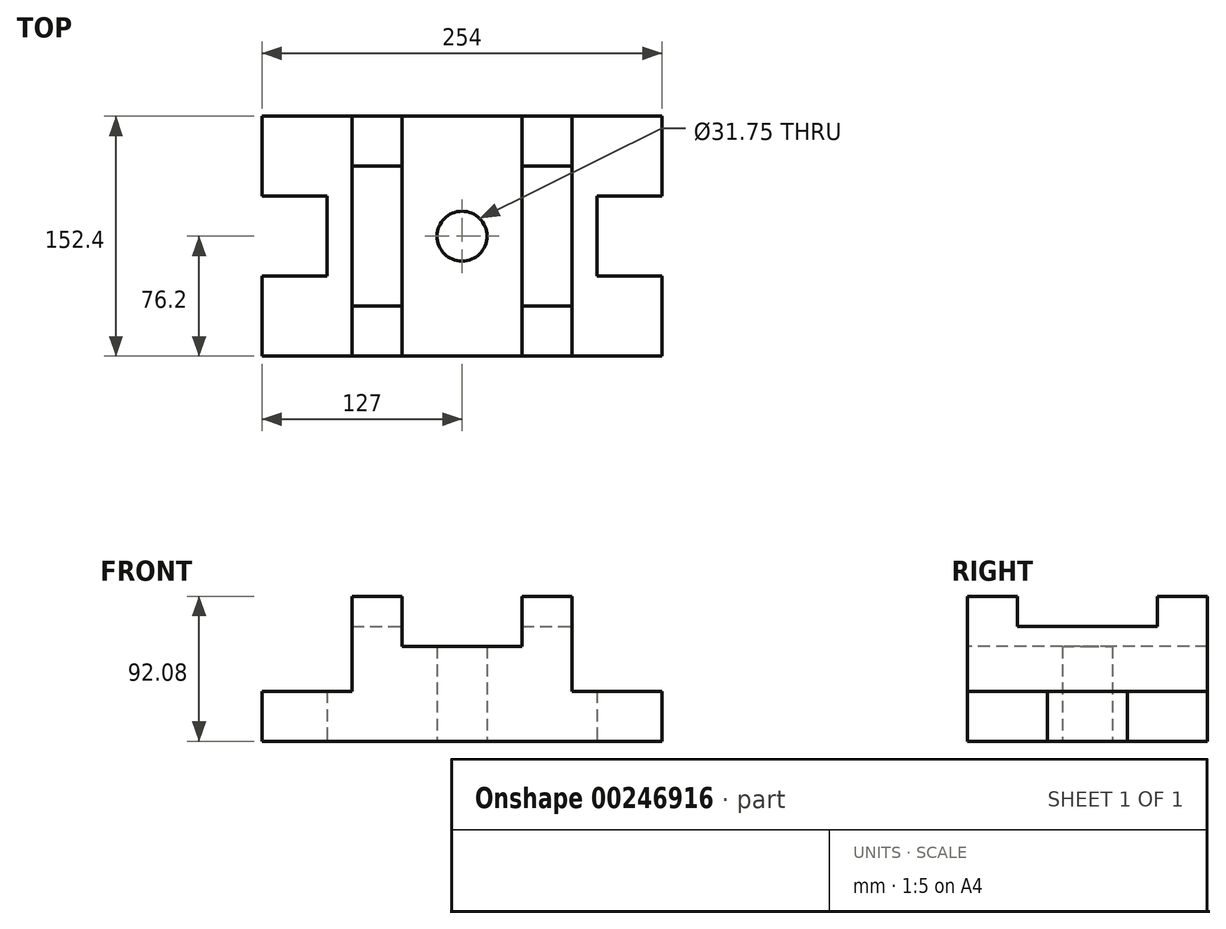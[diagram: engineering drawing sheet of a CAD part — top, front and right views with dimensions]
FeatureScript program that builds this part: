
annotation { "Feature Type Name" : "Feature", "Feature Type Description" : "" }
export const myFeature = defineFeature(function(context is Context, id is Id, definition is map)
    precondition{}
    {
        {
            var Q0;
            Q0=qCreatedBy(makeId("Top.planeOp"),FACE);
            var sketch = newSketch(context, id + "F0", { "sketchPlane" : qUnion([Q0])});
            skCircle(sketch, "E0", {"center": v(0, 0) * mm, "radius": 15.88 * mm});
            skLineSegment(sketch, "E1", {"start": v(-38.1, -76.2) * mm, "end": v(38.1, -76.2) * mm});
            skPoint(sketch, "E2", {"position": v(0, -76.2) * mm});
            skLineSegment(sketch, "E3", {"start": v(-38.1, 76.2) * mm, "end": v(38.1, 76.2) * mm});
            skPoint(sketch, "E4", {"position": v(0, 76.2) * mm});
            skLineSegment(sketch, "E5", {"start": v(-38.1, 76.2) * mm, "end": v(-38.1, -76.2) * mm});
            skLineSegment(sketch, "E6", {"start": v(38.1, 76.2) * mm, "end": v(38.1, -76.2) * mm});
            skLineSegment(sketch, "E7", {"start": v(-38.1, 76.2) * mm, "end": v(-69.85, 76.2) * mm});
            skLineSegment(sketch, "E8", {"start": v(-69.85, 76.2) * mm, "end": v(-69.85, 44.45) * mm});
            skLineSegment(sketch, "E9", {"start": v(-69.85, 44.45) * mm, "end": v(-38.1, 44.45) * mm});
            skLineSegment(sketch, "E10", {"start": v(-38.1, 44.45) * mm, "end": v(-38.1, 76.2) * mm});
            skLineSegment(sketch, "E11", {"start": v(38.1, 76.2) * mm, "end": v(69.85, 76.2) * mm});
            skLineSegment(sketch, "E12", {"start": v(69.85, 76.2) * mm, "end": v(69.85, 44.45) * mm});
            skLineSegment(sketch, "E13", {"start": v(69.85, 44.45) * mm, "end": v(38.1, 44.45) * mm});
            skLineSegment(sketch, "E14", {"start": v(38.1, 44.45) * mm, "end": v(38.1, 76.2) * mm});
            skLineSegment(sketch, "E15", {"start": v(-38.1, -76.2) * mm, "end": v(-69.85, -76.2) * mm});
            skLineSegment(sketch, "E16", {"start": v(-69.85, -76.2) * mm, "end": v(-69.85, -44.45) * mm});
            skLineSegment(sketch, "E17", {"start": v(-69.85, -44.45) * mm, "end": v(-38.1, -44.45) * mm});
            skLineSegment(sketch, "E18", {"start": v(-38.1, -44.45) * mm, "end": v(-38.1, -76.2) * mm});
            skLineSegment(sketch, "E19", {"start": v(38.1, -76.2) * mm, "end": v(69.85, -76.2) * mm});
            skLineSegment(sketch, "E20", {"start": v(69.85, -76.2) * mm, "end": v(69.85, -44.45) * mm});
            skLineSegment(sketch, "E21", {"start": v(69.85, -44.45) * mm, "end": v(38.1, -44.45) * mm});
            skLineSegment(sketch, "E22", {"start": v(38.1, -44.45) * mm, "end": v(38.1, -76.2) * mm});
            skLineSegment(sketch, "E23", {"start": v(-69.85, 44.45) * mm, "end": v(-69.85, -44.45) * mm});
            skLineSegment(sketch, "E24", {"start": v(69.85, 44.45) * mm, "end": v(69.85, -44.45) * mm});
            skLineSegment(sketch, "E25", {"start": v(69.85, 76.2) * mm, "end": v(127, 76.2) * mm});
            skLineSegment(sketch, "E26", {"start": v(127, 76.2) * mm, "end": v(127, 25.4) * mm});
            skLineSegment(sketch, "E27", {"start": v(127, -76.2) * mm, "end": v(69.85, -76.2) * mm});
            skLineSegment(sketch, "E28", {"start": v(-69.85, 76.2) * mm, "end": v(-127, 76.2) * mm});
            skLineSegment(sketch, "E29", {"start": v(-127, 76.2) * mm, "end": v(-127, 25.4) * mm});
            skLineSegment(sketch, "E30", {"start": v(-127, -76.2) * mm, "end": v(-69.85, -76.2) * mm});
            skLineSegment(sketch, "E31", {"start": v(127, 25.4) * mm, "end": v(85.72, 25.4) * mm});
            skLineSegment(sketch, "E32", {"start": v(85.72, 25.4) * mm, "end": v(85.72, -25.4) * mm});
            skLineSegment(sketch, "E33", {"start": v(85.72, -25.4) * mm, "end": v(127, -25.4) * mm});
            skLineSegment(sketch, "E34", {"start": v(-127, 25.4) * mm, "end": v(-85.73, 25.4) * mm});
            skLineSegment(sketch, "E35", {"start": v(-85.73, 25.4) * mm, "end": v(-85.73, -25.4) * mm});
            skLineSegment(sketch, "E36", {"start": v(-85.73, -25.4) * mm, "end": v(-127, -25.4) * mm});
            skLineSegment(sketch, "E37.trimOffspring", {"start": v(-127, -25.4) * mm, "end": v(-127, -76.2) * mm});
            skLineSegment(sketch, "E38.trimOffspring", {"start": v(127, -25.4) * mm, "end": v(127, -76.2) * mm});
            skSolve(sketch);
        }
        {
            var Q0;
            Q0=makeQuery(id+"F0.imprint","IMPRINT",FACE,{"disambiguationData":[TD([[makeQuery(id+"F0.imprint","IMPRINT",EDGE,{"derivedFrom":sQuery(id+"F0.wireOp",EDGE,"E7")}),1.0]])]});
            var Q1;
            Q1=makeQuery(id+"F0.imprint","IMPRINT",FACE,{"disambiguationData":[TD([[makeQuery(id+"F0.imprint","IMPRINT",EDGE,{"derivedFrom":sQuery(id+"F0.wireOp",EDGE,"E11")}),-1.0]])]});
            var Q2;
            Q2=makeQuery(id+"F0.imprint","IMPRINT",FACE,{"disambiguationData":[TD([[makeQuery(id+"F0.imprint","IMPRINT",EDGE,{"derivedFrom":sQuery(id+"F0.wireOp",EDGE,"E15")}),-1.0]])]});
            var Q3;
            Q3=makeQuery(id+"F0.imprint","IMPRINT",FACE,{"disambiguationData":[TD([[makeQuery(id+"F0.imprint","IMPRINT",EDGE,{"derivedFrom":sQuery(id+"F0.wireOp",EDGE,"E19")}),1.0]])]});
            var Q4;
            Q4=makeQuery(id+"F0.imprint","IMPRINT",FACE,{"disambiguationData":[TD([[makeQuery(id+"F0.imprint","IMPRINT",EDGE,{"derivedFrom":sQuery(id+"F0.wireOp",EDGE,"E8")}),-1.0]])]});
            var Q5;
            Q5=makeQuery(id+"F0.imprint","IMPRINT",FACE,{"disambiguationData":[TD([[makeQuery(id+"F0.imprint","IMPRINT",EDGE,{"derivedFrom":sQuery(id+"F0.wireOp",EDGE,"E12")}),1.0]])]});
            var Q6;
            Q6=makeQuery(id+"F0.imprint","IMPRINT",FACE,{"disambiguationData":[TD([[makeQuery(id+"F0.imprint","IMPRINT",EDGE,{"derivedFrom":sQuery(id+"F0.wireOp",EDGE,"E0")}),-1.0]])]});
            var Q7;
            Q7=makeQuery(id+"F0.imprint","IMPRINT",FACE,{"disambiguationData":[TD([[makeQuery(id+"F0.imprint","IMPRINT",EDGE,{"derivedFrom":sQuery(id+"F0.wireOp",EDGE,"E5")}),-1.0]])]});
            var Q8;
            Q8=makeQuery(id+"F0.imprint","IMPRINT",FACE,{"disambiguationData":[TD([[makeQuery(id+"F0.imprint","IMPRINT",EDGE,{"derivedFrom":sQuery(id+"F0.wireOp",EDGE,"E6")}),1.0]])]});
            extrude(context, id + "F1", {"entities" : qUnion([Q0, Q1, Q2, Q3, Q4, Q5, Q6, Q7, Q8]), "depth" : 92.07 * mm});
        }
        {
            var Q0;
            Q0=makeQuery(id+"F1.opExtrude","SWEPT_FACE",FACE,{"disambiguationData":[OSD([sQuery(id+"F0.wireOp",EDGE,"E1"),sQuery(id+"F0.wireOp",EDGE,"E15"),sQuery(id+"F0.wireOp",EDGE,"E19"),sQuery(id+"F0.wireOp",EDGE,"E27"),sQuery(id+"F0.wireOp",EDGE,"E30")])]});
            var sketch = newSketch(context, id + "F2", { "sketchPlane" : qUnion([Q0])});
            skLineSegment(sketch, "E39", {"start": v(-127, 0) * mm, "end": v(-127, 31.75) * mm});
            skLineSegment(sketch, "E40", {"start": v(-127, 31.75) * mm, "end": v(-69.85, 31.75) * mm});
            skLineSegment(sketch, "E41", {"start": v(-69.85, 31.75) * mm, "end": v(-69.85, 0) * mm});
            skLineSegment(sketch, "E42", {"start": v(127, 0) * mm, "end": v(127, 31.75) * mm});
            skLineSegment(sketch, "E43", {"start": v(127, 31.75) * mm, "end": v(69.85, 31.75) * mm});
            skLineSegment(sketch, "E44", {"start": v(69.85, 31.75) * mm, "end": v(69.85, 0) * mm});
            skLineSegment(sketch, "E45", {"start": v(69.85, 0) * mm, "end": v(127, 0) * mm});
            skLineSegment(sketch, "E46", {"start": v(-69.85, 0) * mm, "end": v(-127, 0) * mm});
            skLineSegment(sketch, "E47.bottom", {"start": v(-127, 31.75) * mm, "end": v(-127, 31.75) * mm});
            skLineSegment(sketch, "E47.top", {"start": v(-127, 92.08) * mm, "end": v(-127, 92.08) * mm});
            skLineSegment(sketch, "E47.left", {"start": v(-127, 31.75) * mm, "end": v(-127, 92.08) * mm});
            skLineSegment(sketch, "E47.right", {"start": v(-127, 31.75) * mm, "end": v(-127, 92.08) * mm});
            skLineSegment(sketch, "E48", {"start": v(-69.85, 31.75) * mm, "end": v(-69.85, 92.08) * mm});
            skLineSegment(sketch, "E49", {"start": v(-69.85, 92.08) * mm, "end": v(-127, 92.08) * mm});
            skLineSegment(sketch, "E50", {"start": v(127, 31.75) * mm, "end": v(127, 92.08) * mm});
            skLineSegment(sketch, "E51", {"start": v(127, 92.07) * mm, "end": v(69.85, 92.07) * mm});
            skLineSegment(sketch, "E52", {"start": v(69.85, 92.07) * mm, "end": v(69.85, 31.75) * mm});
            skLineSegment(sketch, "E53", {"start": v(-69.85, 92.08) * mm, "end": v(-38.1, 92.08) * mm});
            skLineSegment(sketch, "E54", {"start": v(-38.1, 92.08) * mm, "end": v(-38.1, 60.24) * mm});
            skLineSegment(sketch, "E55", {"start": v(-38.1, 60.24) * mm, "end": v(38.1, 60.24) * mm});
            skLineSegment(sketch, "E56", {"start": v(38.1, 60.24) * mm, "end": v(38.1, 92.08) * mm});
            skLineSegment(sketch, "E57", {"start": v(38.1, 92.08) * mm, "end": v(69.85, 92.07) * mm});
            skLineSegment(sketch, "E58", {"start": v(-38.1, 92.08) * mm, "end": v(38.1, 92.08) * mm});
            skSolve(sketch);
        }
        {
            var Q0;
            Q0=makeQuery(id+"F2.imprint","IMPRINT",FACE,{"disambiguationData":[TD([[makeQuery(id+"F2.imprint","IMPRINT",EDGE,{"derivedFrom":sQuery(id+"F2.wireOp",EDGE,"E54")}),1.0]])]});
            var Q1;
            Q1=makeQuery(id+"F2.imprint","IMPRINT",FACE,{"disambiguationData":[TD([[makeQuery(id+"F2.imprint","IMPRINT",EDGE,{"derivedFrom":sQuery(id+"F2.wireOp",EDGE,"E40")}),1.0]])]});
            var Q2;
            Q2=makeQuery(id+"F2.imprint","IMPRINT",FACE,{"disambiguationData":[TD([[makeQuery(id+"F2.imprint","IMPRINT",EDGE,{"derivedFrom":sQuery(id+"F2.wireOp",EDGE,"E43")}),-1.0]])]});
            extrude(context, id + "F3", {"entities" : qUnion([Q0, Q1, Q2]), "operationType" : NewBodyOperationType.REMOVE, "endBound" : BoundingType.THROUGH_ALL, "oppositeDirection" : true, "depth" : 25.4 * mm});
        }
        {
            var Q0;
            Q0=makeQuery(id+"F3.boolean.opBoolean","COPY",FACE,{"derivedFrom":makeQuery(id+"F3.opExtrude","SWEPT_FACE",FACE,{"disambiguationData":[OSD([sQuery(id+"F2.wireOp",EDGE,"E52")])]})});
            var sketch = newSketch(context, id + "F4", { "sketchPlane" : qUnion([Q0])});
            skLineSegment(sketch, "E59", {"start": v(-76.2, 92.08) * mm, "end": v(-44.45, 92.08) * mm});
            skLineSegment(sketch, "E60", {"start": v(-44.45, 92.08) * mm, "end": v(-44.45, 73.03) * mm});
            skLineSegment(sketch, "E61", {"start": v(-44.45, 73.03) * mm, "end": v(44.45, 73.03) * mm});
            skLineSegment(sketch, "E62", {"start": v(44.45, 73.03) * mm, "end": v(44.45, 92.08) * mm});
            skLineSegment(sketch, "E63", {"start": v(44.45, 92.08) * mm, "end": v(-44.45, 92.08) * mm});
            skLineSegment(sketch, "E64", {"start": v(44.45, 92.08) * mm, "end": v(76.2, 92.08) * mm});
            skSolve(sketch);
        }
        {
            var Q0;
            Q0=makeQuery(id+"F4.imprint","IMPRINT",FACE,{"disambiguationData":[TD([[makeQuery(id+"F4.imprint","IMPRINT",EDGE,{"derivedFrom":sQuery(id+"F4.wireOp",EDGE,"E60")}),1.0]])]});
            extrude(context, id + "F5", {"entities" : qUnion([Q0]), "operationType" : NewBodyOperationType.REMOVE, "endBound" : BoundingType.THROUGH_ALL, "oppositeDirection" : true, "depth" : 25.4 * mm});
        }
    });
